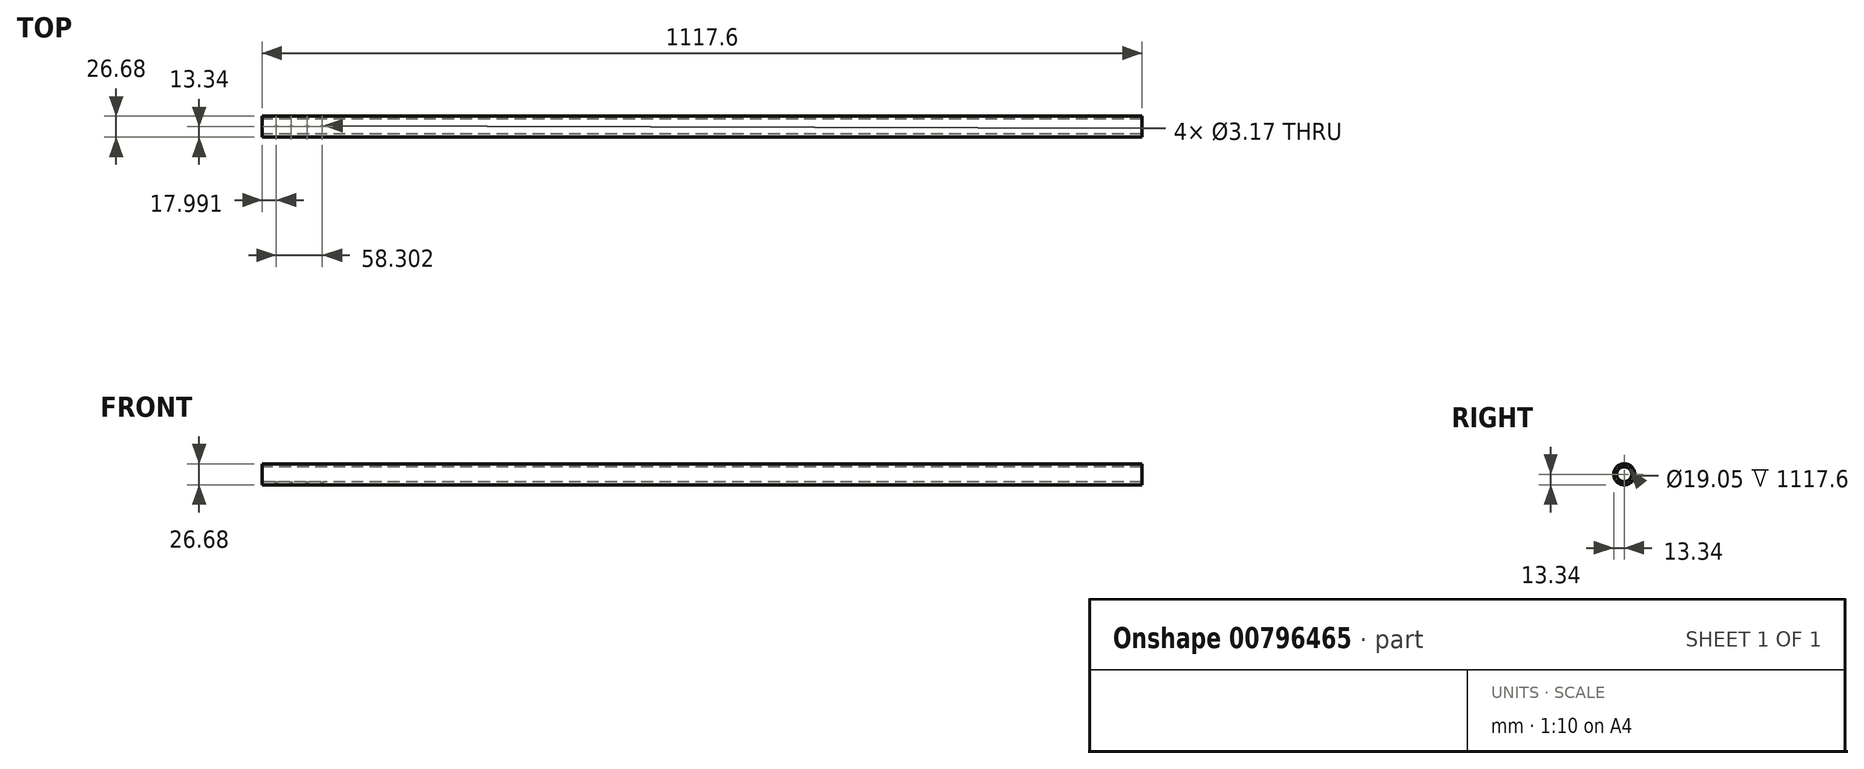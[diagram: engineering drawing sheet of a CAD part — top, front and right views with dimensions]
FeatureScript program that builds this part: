
annotation { "Feature Type Name" : "Feature", "Feature Type Description" : "" }
export const myFeature = defineFeature(function(context is Context, id is Id, definition is map)
    precondition{}
    {
        {
            var Q0;
            Q0=qCreatedBy(makeId("Right.planeOp"),FACE);
            var sketch = newSketch(context, id + "F0", { "sketchPlane" : qUnion([Q0])});
            skCircle(sketch, "E0", {"center": v(0, 0) * mm, "radius": 9.53 * mm});
            skCircle(sketch, "E1.0", {"center": v(0, 0) * mm, "radius": 13.33 * mm});
            skSolve(sketch);
        }
        {
            var Q0;
            Q0=qSketchRegion(id+"F0",true);
            extrude(context, id + "F1", {"entities" : qUnion([Q0]), "depth" : 1117.6 * mm, "offsetDistance" : 25.4 * mm});
        }
        {
            var Q0;
            Q0=qCreatedBy(makeId("Top.planeOp"),FACE);
            var sketch = newSketch(context, id + "F2", { "sketchPlane" : qUnion([Q0])});
            skLineSegment(sketch, "E2", {"start": v(0, 0) * mm, "end": v(1117.6, 0) * mm});
            skPoint(sketch, "E3", {"position": v(18, 0) * mm});
            skPoint(sketch, "E4", {"position": v(36.94, 0) * mm});
            skPoint(sketch, "E5", {"position": v(57.16, 0) * mm});
            skPoint(sketch, "E6", {"position": v(76.3, 0) * mm});
            skSolve(sketch);
        }
        {
            var Q0;
            Q0=sQuery(id+"F2.wireOp",VERTEX,"E3");
            var Q1;
            Q1=makeQuery(id+"F1.opExtrude","SWEPT_BODY",BODY,{"disambiguationData":[OSD([sQuery(id+"F0.wireOp",EDGE,"E0"),sQuery(id+"F0.wireOp",EDGE,"E1.0")])]});
            hole(context, id + "F3", {"style" : HoleStyle.SIMPLE, "endStyle" : HoleEndStyle.BLIND, "holeDiameter" : 3.17 * mm, "majorDiameter" : 6.35 * mm, "holeDepth" : 25.4 * mm, "isTappedThrough" : true, "tappedDepth" : 12.7 * mm, "tapClearance" : 3, "locations" : qUnion([Q0]), "scope" : qUnion([Q1])});
        }
        {
            var Q0;
            Q0=sQuery(id+"F2.wireOp",VERTEX,"E4");
            var Q1;
            Q1=makeQuery(id+"F1.opExtrude","SWEPT_BODY",BODY,{"disambiguationData":[OSD([sQuery(id+"F0.wireOp",EDGE,"E0"),sQuery(id+"F0.wireOp",EDGE,"E1.0")])]});
            hole(context, id + "F4", {"style" : HoleStyle.SIMPLE, "endStyle" : HoleEndStyle.BLIND, "holeDiameter" : 3.17 * mm, "majorDiameter" : 6.35 * mm, "holeDepth" : 25.4 * mm, "isTappedThrough" : true, "tappedDepth" : 12.7 * mm, "tapClearance" : 3, "locations" : qUnion([Q0]), "scope" : qUnion([Q1])});
        }
        {
            var Q0;
            Q0=sQuery(id+"F2.wireOp",VERTEX,"E6");
            var Q1;
            Q1=makeQuery(id+"F1.opExtrude","SWEPT_BODY",BODY,{"disambiguationData":[OSD([sQuery(id+"F0.wireOp",EDGE,"E0"),sQuery(id+"F0.wireOp",EDGE,"E1.0")])]});
            hole(context, id + "F5", {"style" : HoleStyle.SIMPLE, "endStyle" : HoleEndStyle.BLIND, "holeDiameter" : 3.17 * mm, "majorDiameter" : 6.35 * mm, "holeDepth" : 25.4 * mm, "isTappedThrough" : true, "tappedDepth" : 12.7 * mm, "tapClearance" : 3, "locations" : qUnion([Q0]), "scope" : qUnion([Q1])});
        }
        {
            var Q0;
            Q0=sQuery(id+"F2.wireOp",VERTEX,"E5");
            var Q1;
            Q1=makeQuery(id+"F1.opExtrude","SWEPT_BODY",BODY,{"disambiguationData":[OSD([sQuery(id+"F0.wireOp",EDGE,"E0"),sQuery(id+"F0.wireOp",EDGE,"E1.0")])]});
            hole(context, id + "F6", {"style" : HoleStyle.SIMPLE, "endStyle" : HoleEndStyle.BLIND, "holeDiameter" : 3.17 * mm, "majorDiameter" : 6.35 * mm, "holeDepth" : 25.4 * mm, "isTappedThrough" : true, "tappedDepth" : 12.7 * mm, "tapClearance" : 3, "locations" : qUnion([Q0]), "scope" : qUnion([Q1])});
        }
    });
